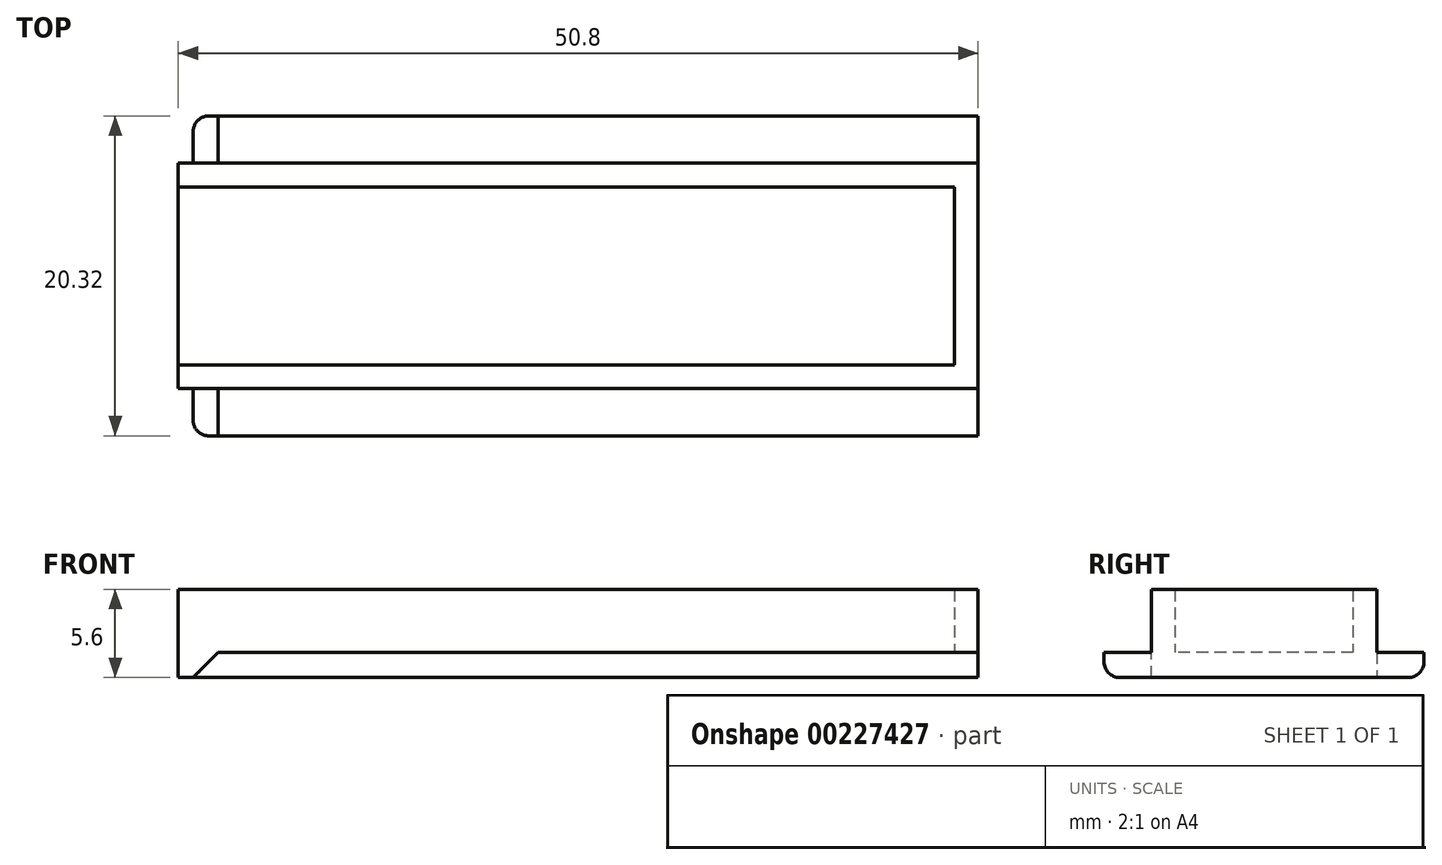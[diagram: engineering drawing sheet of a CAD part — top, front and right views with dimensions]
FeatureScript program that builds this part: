
annotation { "Feature Type Name" : "Feature", "Feature Type Description" : "" }
export const myFeature = defineFeature(function(context is Context, id is Id, definition is map)
    precondition{}
    {
        {
            var Q0;
            Q0=qCreatedBy(makeId("Top.planeOp"),FACE);
            var sketch = newSketch(context, id + "F0", { "sketchPlane" : qUnion([Q0])});
            skLineSegment(sketch, "E0.bottom", {"start": v(-25.4, 10.16) * mm, "end": v(25.4, 10.16) * mm});
            skLineSegment(sketch, "E0.top", {"start": v(-25.4, -10.16) * mm, "end": v(25.4, -10.16) * mm});
            skLineSegment(sketch, "E0.left", {"start": v(-25.4, 10.16) * mm, "end": v(-25.4, -10.16) * mm});
            skLineSegment(sketch, "E0.right", {"start": v(25.4, 10.16) * mm, "end": v(25.4, -10.16) * mm});
            skPoint(sketch, "E0.middle", {"position": v(0, 0) * mm});
            skSolve(sketch);
        }
        {
            var Q0;
            Q0 = qSketchRegion(id + "F0", true);
            extrude(context, id + "F1", {"entities" : qUnion([Q0]), "depth" : 1.6 * mm});
        }
        {
            var Q0;
            Q0=makeQuery(id+"F1.opExtrude","CAP_FACE",FACE,{"disambiguationData":[OSD([sQuery(id+"F0.wireOp",EDGE,"E0.bottom"),sQuery(id+"F0.wireOp",EDGE,"E0.top"),sQuery(id+"F0.wireOp",EDGE,"E0.left"),sQuery(id+"F0.wireOp",EDGE,"E0.right")])],"isStart":false});
            var sketch = newSketch(context, id + "F2", { "sketchPlane" : qUnion([Q0])});
            skLineSegment(sketch, "E1.bottom", {"start": v(-25.4, 7.16) * mm, "end": v(25.4, 7.16) * mm});
            skLineSegment(sketch, "E1.top", {"start": v(-25.4, 5.66) * mm, "end": v(25.4, 5.66) * mm});
            skLineSegment(sketch, "E1.left", {"start": v(-25.4, 7.16) * mm, "end": v(-25.4, 5.66) * mm});
            skLineSegment(sketch, "E1.right", {"start": v(25.4, 7.16) * mm, "end": v(25.4, 5.66) * mm});
            skLineSegment(sketch, "E2.bottom", {"start": v(-25.4, -5.66) * mm, "end": v(25.4, -5.66) * mm});
            skLineSegment(sketch, "E2.top", {"start": v(-25.4, -7.16) * mm, "end": v(25.4, -7.16) * mm});
            skLineSegment(sketch, "E2.left", {"start": v(-25.4, -5.66) * mm, "end": v(-25.4, -7.16) * mm});
            skLineSegment(sketch, "E2.right", {"start": v(25.4, -5.66) * mm, "end": v(25.4, -7.16) * mm});
            skLineSegment(sketch, "E3.bottom", {"start": v(23.9, 5.66) * mm, "end": v(25.4, 5.66) * mm});
            skLineSegment(sketch, "E3.top", {"start": v(23.9, -5.66) * mm, "end": v(25.4, -5.66) * mm});
            skLineSegment(sketch, "E3.left", {"start": v(23.9, 5.66) * mm, "end": v(23.9, -5.66) * mm});
            skLineSegment(sketch, "E3.right", {"start": v(25.4, 5.66) * mm, "end": v(25.4, -5.66) * mm});
            skSolve(sketch);
        }
        {
            var Q0;
            Q0 = qSketchRegion(id + "F2", true);
            extrude(context, id + "F3", {"entities" : qUnion([Q0]), "operationType" : NewBodyOperationType.ADD, "depth" : 4 * mm});
        }
        {
            var Q0;
            Q0=makeQuery(id+"F1.opExtrude","CAP_EDGE",EDGE,{"disambiguationData":[OSD([sQuery(id+"F0.wireOp",EDGE,"E0.top")])],"isStart":true});
            var Q1;
            Q1=makeQuery(id+"F1.opExtrude","CAP_EDGE",EDGE,{"disambiguationData":[OSD([sQuery(id+"F0.wireOp",EDGE,"E0.bottom")])],"isStart":true});
            fillet(context, id + "F4", {"entities" : qUnion([Q0, Q1]), "radius" : 1 * mm, "tangentPropagation" : true, "allowEdgeOverflow" : false});
        }
        {
            var Q0;
            {var subQ0=sQuery(id+"F0.wireOp",EDGE,"E0.left");var subQ1=sQuery(id+"F0.wireOp",EDGE,"E0.bottom");Q0=makeQuery(id+"F3.boolean.opBoolean","SPLIT",EDGE,{"disambiguationData":[TD([makeQuery(id+"F1.opExtrude","SWEPT_FACE",FACE,{"disambiguationData":[OSD([subQ1])]})])],"derivedFrom":makeQuery(id+"F1.opExtrude","CAP_EDGE",EDGE,{"disambiguationData":[OSD([subQ0])],"isStart":false})});}
            var Q1;
            {var subQ0=sQuery(id+"F0.wireOp",EDGE,"E0.left");var subQ1=sQuery(id+"F0.wireOp",EDGE,"E0.top");Q1=makeQuery(id+"F3.boolean.opBoolean","SPLIT",EDGE,{"disambiguationData":[TD([makeQuery(id+"F1.opExtrude","SWEPT_FACE",FACE,{"disambiguationData":[OSD([subQ1])]})])],"derivedFrom":makeQuery(id+"F1.opExtrude","CAP_EDGE",EDGE,{"disambiguationData":[OSD([subQ0])],"isStart":false})});}
            chamfer(context, id + "F5", {"entities" : qUnion([Q0, Q1]), "width" : 2.54 * mm, "tangentPropagation" : true});
        }
    });
